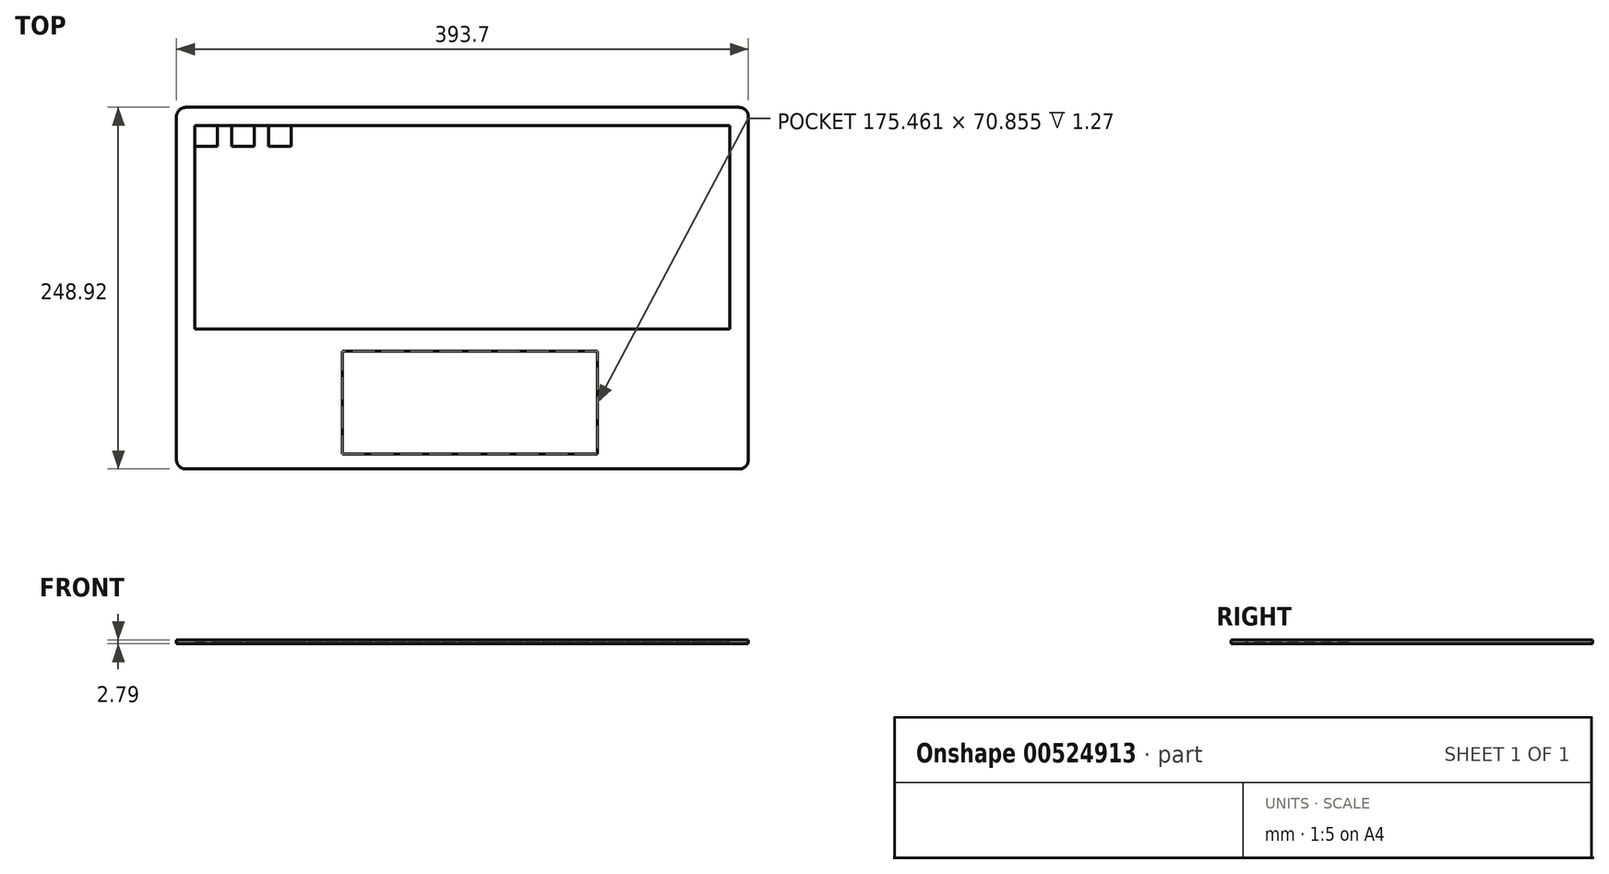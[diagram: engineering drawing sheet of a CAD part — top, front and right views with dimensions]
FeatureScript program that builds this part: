
annotation { "Feature Type Name" : "Feature", "Feature Type Description" : "" }
export const myFeature = defineFeature(function(context is Context, id is Id, definition is map)
    precondition{}
    {
        {
            var Q0;
            Q0=qCreatedBy(makeId("Top.planeOp"),FACE);
            var sketch = newSketch(context, id + "F0", { "sketchPlane" : qUnion([Q0])});
            skLineSegment(sketch, "E0.bottom", {"start": v(185.32, 131.4) * mm, "end": v(-195.68, 131.4) * mm});
            skLineSegment(sketch, "E0.top", {"start": v(185.32, -117.52) * mm, "end": v(-195.68, -117.52) * mm});
            skLineSegment(sketch, "E0.left", {"start": v(191.67, 125.05) * mm, "end": v(191.67, -111.17) * mm});
            skLineSegment(sketch, "E0.right", {"start": v(-202.03, 125.05) * mm, "end": v(-202.03, -111.17) * mm});
            skPoint(sketch, "E1.visualSharp", {"position": v(-202.03, 131.4) * mm});
            skArc(sketch, "E1.filletArc", {"start": v(-195.68, 131.4) * mm, "mid": v(-200.17, 129.54) * mm, "end": v(-202.03, 125.05) * mm});
            skPoint(sketch, "E2.visualSharp", {"position": v(-202.03, -117.52) * mm});
            skArc(sketch, "E2.filletArc", {"start": v(-202.03, -111.17) * mm, "mid": v(-200.17, -115.66) * mm, "end": v(-195.68, -117.52) * mm});
            skPoint(sketch, "E3.visualSharp", {"position": v(191.67, -117.52) * mm});
            skArc(sketch, "E3.filletArc", {"start": v(185.32, -117.52) * mm, "mid": v(189.8, -115.66) * mm, "end": v(191.67, -111.17) * mm});
            skPoint(sketch, "E4.visualSharp", {"position": v(191.67, 131.4) * mm});
            skArc(sketch, "E4.filletArc", {"start": v(191.67, 125.05) * mm, "mid": v(189.8, 129.54) * mm, "end": v(185.32, 131.4) * mm});
            skSolve(sketch);
        }
        {
            var Q0;
            Q0=makeQuery(id+"F0.imprint","IMPRINT",FACE,{"disambiguationData":[TD([[makeQuery(id+"F0.imprint","IMPRINT",EDGE,{"derivedFrom":sQuery(id+"F0.wireOp",EDGE,"E0.bottom")}),1.0]])]});
            extrude(context, id + "F1", {"entities" : qUnion([Q0]), "depth" : 2.8 * mm, "offsetDistance" : 25.4 * mm});
        }
        {
            var Q0;
            Q0=makeQuery(id+"F1.opExtrude","CAP_FACE",FACE,{"disambiguationData":[OSD([sQuery(id+"F0.wireOp",EDGE,"E0.bottom"),sQuery(id+"F0.wireOp",EDGE,"E0.top"),sQuery(id+"F0.wireOp",EDGE,"E0.left"),sQuery(id+"F0.wireOp",EDGE,"E0.right"),sQuery(id+"F0.wireOp",EDGE,"E1.filletArc"),sQuery(id+"F0.wireOp",EDGE,"E2.filletArc"),sQuery(id+"F0.wireOp",EDGE,"E3.filletArc"),sQuery(id+"F0.wireOp",EDGE,"E4.filletArc")])],"isStart":false});
            var sketch = newSketch(context, id + "F2", { "sketchPlane" : qUnion([Q0])});
            skLineSegment(sketch, "E5.bottom", {"start": v(-189.33, 118.7) * mm, "end": v(178.97, 118.7) * mm});
            skLineSegment(sketch, "E5.top", {"start": v(-189.33, -21.27) * mm, "end": v(178.97, -21.27) * mm});
            skLineSegment(sketch, "E5.left", {"start": v(-189.33, 118.7) * mm, "end": v(-189.33, -21.27) * mm});
            skLineSegment(sketch, "E5.right", {"start": v(178.97, 118.7) * mm, "end": v(178.97, -21.27) * mm});
            skSolve(sketch);
        }
        {
            var Q0;
            Q0=makeQuery(id+"F2.imprint","IMPRINT",FACE,{"disambiguationData":[TD([[makeQuery(id+"F2.imprint","IMPRINT",EDGE,{"derivedFrom":sQuery(id+"F2.wireOp",EDGE,"E5.bottom")}),-1.0]])]});
            extrude(context, id + "F3", {"entities" : qUnion([Q0]), "operationType" : NewBodyOperationType.REMOVE, "oppositeDirection" : true, "depth" : 0.76 * mm, "offsetDistance" : 25.4 * mm});
        }
        {
            var Q0;
            Q0=makeQuery(id+"F1.opExtrude","CAP_FACE",FACE,{"disambiguationData":[OSD([sQuery(id+"F0.wireOp",EDGE,"E0.bottom"),sQuery(id+"F0.wireOp",EDGE,"E0.top"),sQuery(id+"F0.wireOp",EDGE,"E0.left"),sQuery(id+"F0.wireOp",EDGE,"E0.right"),sQuery(id+"F0.wireOp",EDGE,"E1.filletArc"),sQuery(id+"F0.wireOp",EDGE,"E2.filletArc"),sQuery(id+"F0.wireOp",EDGE,"E3.filletArc"),sQuery(id+"F0.wireOp",EDGE,"E4.filletArc")])],"isStart":false});
            var sketch = newSketch(context, id + "F4", { "sketchPlane" : qUnion([Q0])});
            skLineSegment(sketch, "E6.bottom", {"start": v(-87.73, -36.5) * mm, "end": v(87.73, -36.5) * mm});
            skLineSegment(sketch, "E6.top", {"start": v(-87.73, -107.36) * mm, "end": v(87.73, -107.36) * mm});
            skLineSegment(sketch, "E6.left", {"start": v(-87.73, -36.5) * mm, "end": v(-87.73, -107.36) * mm});
            skLineSegment(sketch, "E6.right", {"start": v(87.73, -36.5) * mm, "end": v(87.73, -107.36) * mm});
            skPoint(sketch, "E6.middle", {"position": v(0, -71.93) * mm});
            skSolve(sketch);
        }
        {
            var Q0;
            Q0 = qSketchRegion(id + "F4", true);
            extrude(context, id + "F5", {"entities" : qUnion([Q0]), "operationType" : NewBodyOperationType.REMOVE, "oppositeDirection" : true, "depth" : 1.27 * mm, "offsetDistance" : 25.4 * mm});
        }
        {
            var Q0;
            Q0=makeQuery(id+"F3.boolean.opBoolean","COPY",FACE,{"derivedFrom":makeQuery(id+"F3.opExtrude","CAP_FACE",FACE,{"disambiguationData":[OSD([sQuery(id+"F2.wireOp",EDGE,"E5.bottom"),sQuery(id+"F2.wireOp",EDGE,"E5.top"),sQuery(id+"F2.wireOp",EDGE,"E5.left"),sQuery(id+"F2.wireOp",EDGE,"E5.right")])],"isStart":false})});
            var sketch = newSketch(context, id + "F6", { "sketchPlane" : qUnion([Q0])});
            skLineSegment(sketch, "E7.bottom", {"start": v(-189.33, 118.7) * mm, "end": v(-174, 118.7) * mm});
            skLineSegment(sketch, "E7.top", {"start": v(-189.33, 104.58) * mm, "end": v(-174, 104.58) * mm});
            skLineSegment(sketch, "E7.left", {"start": v(-189.33, 118.7) * mm, "end": v(-189.33, 104.58) * mm});
            skLineSegment(sketch, "E7.right", {"start": v(-174, 118.7) * mm, "end": v(-174, 104.58) * mm});
            skLineSegment(sketch, "E8.1.0.0", {"start": v(-163.93, 118.7) * mm, "end": v(-148.6, 118.7) * mm});
            skLineSegment(sketch, "E8.1.0.1", {"start": v(-163.93, 118.7) * mm, "end": v(-163.93, 104.58) * mm});
            skLineSegment(sketch, "E8.1.0.2", {"start": v(-163.93, 104.58) * mm, "end": v(-148.6, 104.58) * mm});
            skLineSegment(sketch, "E8.1.0.3", {"start": v(-148.6, 118.7) * mm, "end": v(-148.6, 104.58) * mm});
            skLineSegment(sketch, "E8.2.0.0", {"start": v(-138.53, 118.7) * mm, "end": v(-123.2, 118.7) * mm});
            skLineSegment(sketch, "E8.2.0.1", {"start": v(-138.53, 118.7) * mm, "end": v(-138.53, 104.58) * mm});
            skLineSegment(sketch, "E8.2.0.2", {"start": v(-138.53, 104.58) * mm, "end": v(-123.2, 104.58) * mm});
            skLineSegment(sketch, "E8.2.0.3", {"start": v(-123.2, 118.7) * mm, "end": v(-123.2, 104.58) * mm});
            skLineSegment(sketch, "E8.direction1", {"start": v(-189.33, 118.7) * mm, "end": v(-163.93, 118.7) * mm, "construction": true});
            skSolve(sketch);
        }
        {
            var Q0;
            Q0=makeQuery(id+"F6.imprint","IMPRINT",FACE,{"disambiguationData":[TD([[makeQuery(id+"F6.imprint","IMPRINT",EDGE,{"derivedFrom":sQuery(id+"F6.wireOp",EDGE,"E7.bottom")}),-1.0]])]});
            var Q1;
            Q1=makeQuery(id+"F6.imprint","IMPRINT",FACE,{"disambiguationData":[TD([[makeQuery(id+"F6.imprint","IMPRINT",EDGE,{"derivedFrom":sQuery(id+"F6.wireOp",EDGE,"E8.1.0.0")}),-1.0]])]});
            var Q2;
            Q2=makeQuery(id+"F6.imprint","IMPRINT",FACE,{"disambiguationData":[TD([[makeQuery(id+"F6.imprint","IMPRINT",EDGE,{"derivedFrom":sQuery(id+"F6.wireOp",EDGE,"E8.2.0.0")}),-1.0]])]});
            extrude(context, id + "F7", {"entities" : qUnion([Q0, Q1, Q2]), "operationType" : NewBodyOperationType.ADD, "depth" : 0.5 * mm, "offsetDistance" : 25.4 * mm});
        }
    });
